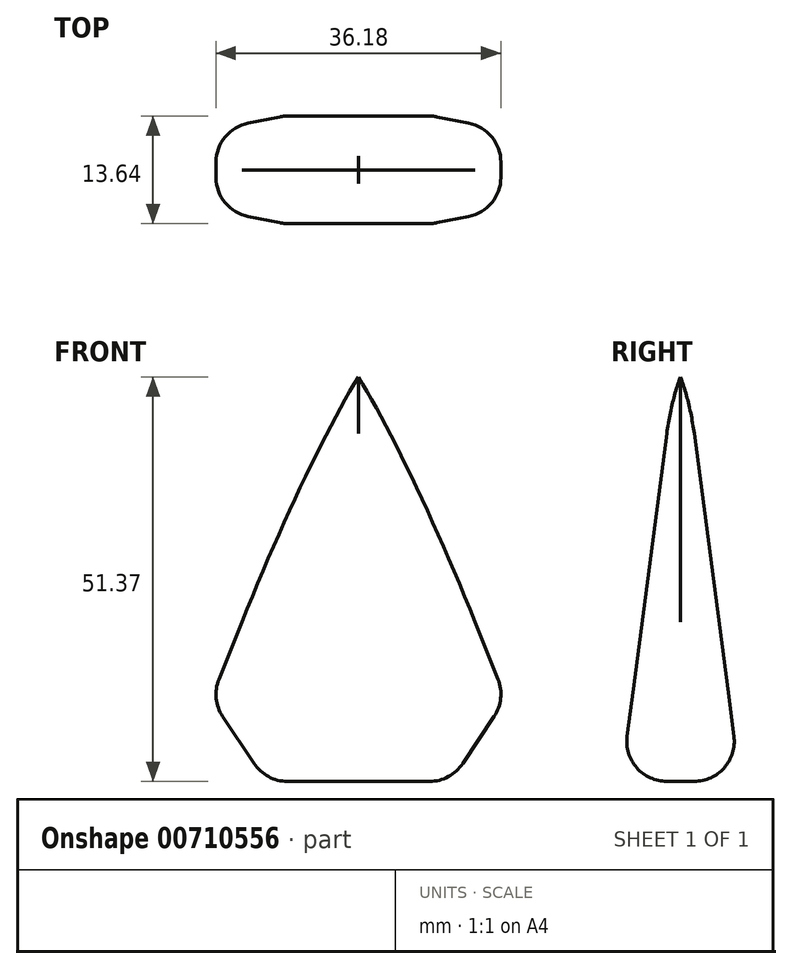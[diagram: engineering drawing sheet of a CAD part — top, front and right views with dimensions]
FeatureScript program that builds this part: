
annotation { "Feature Type Name" : "Feature", "Feature Type Description" : "" }
export const myFeature = defineFeature(function(context is Context, id is Id, definition is map)
    precondition{}
    {
        {
            var Q0;
            Q0=qCreatedBy(makeId("Front.planeOp"),FACE);
            var sketch = newSketch(context, id + "F0", { "sketchPlane" : qUnion([Q0])});
            skLineSegment(sketch, "E0", {"start": v(0, -118.48) * mm, "end": v(-11.74, -118.48) * mm});
            skLineSegment(sketch, "E1", {"start": v(-11.74, -118.48) * mm, "end": v(-18.73, -108) * mm});
            skLineSegment(sketch, "E2", {"start": v(-18.73, -108) * mm, "end": v(0, -61.33) * mm});
            skLineSegment(sketch, "E3", {"start": v(0, -61.33) * mm, "end": v(0, -68.6) * mm});
            skLineSegment(sketch, "E4.MirrorCS", {"start": v(18.73, -108) * mm, "end": v(0, -61.33) * mm});
            skLineSegment(sketch, "E5.MirrorCS", {"start": v(11.74, -118.48) * mm, "end": v(18.73, -108) * mm});
            skLineSegment(sketch, "E6.MirrorCS", {"start": v(0, -118.48) * mm, "end": v(11.74, -118.48) * mm});
            skSolve(sketch);
        }
        {
            var Q0;
            Q0=makeQuery(id+"F0.imprint","IMPRINT",FACE,{"disambiguationData":[TD([[makeQuery(id+"F0.imprint","IMPRINT",EDGE,{"derivedFrom":sQuery(id+"F0.wireOp",EDGE,"E0")}),-1.0]])]});
            extrude(context, id + "F1", {"entities" : qUnion([Q0]), "depth" : 7.62 * mm, "offsetDistance" : 25.4 * mm});
        }
        {
            var Q0;
            Q0=makeQuery(id+"F1.opExtrude","CAP_FACE",FACE,{"disambiguationData":[OSD([sQuery(id+"F0.wireOp",EDGE,"E0"),sQuery(id+"F0.wireOp",EDGE,"E1"),sQuery(id+"F0.wireOp",EDGE,"E2"),sQuery(id+"F0.wireOp",EDGE,"E4.MirrorCS"),sQuery(id+"F0.wireOp",EDGE,"E5.MirrorCS"),sQuery(id+"F0.wireOp",EDGE,"E6.MirrorCS")])],"isStart":true});
            extrude(context, id + "F2", {"entities" : qUnion([Q0]), "operationType" : NewBodyOperationType.ADD, "depth" : 7.62 * mm, "offsetDistance" : 25.4 * mm});
        }
        {
            var Q0;
            Q0=qCreatedBy(makeId("Right.planeOp"),FACE);
            var sketch = newSketch(context, id + "F3", { "sketchPlane" : qUnion([Q0])});
            skLineSegment(sketch, "E7", {"start": v(0, -61.02) * mm, "end": v(-7.8, -120.59) * mm});
            skLineSegment(sketch, "E8", {"start": v(0, -61.02) * mm, "end": v(0, -70.15) * mm});
            skLineSegment(sketch, "E9.MirrorCS", {"start": v(0, -61.02) * mm, "end": v(7.8, -120.59) * mm});
            skLineSegment(sketch, "E10", {"start": v(7.8, -120.59) * mm, "end": v(-7.8, -120.59) * mm});
            skLineSegment(sketch, "E11", {"start": v(-14.15, -128.32) * mm, "end": v(-14.15, -55.45) * mm});
            skLineSegment(sketch, "E12", {"start": v(-14.15, -55.45) * mm, "end": v(17.72, -55.45) * mm});
            skLineSegment(sketch, "E13", {"start": v(17.72, -55.45) * mm, "end": v(15.55, -132.5) * mm});
            skLineSegment(sketch, "E14", {"start": v(15.55, -132.5) * mm, "end": v(-14.15, -128.32) * mm});
            skSolve(sketch);
        }
        {
            var Q0;
            Q0=makeQuery(id+"F3.imprint","IMPRINT",FACE,{"disambiguationData":[TD([[makeQuery(id+"F3.imprint","IMPRINT",EDGE,{"derivedFrom":sQuery(id+"F3.wireOp",EDGE,"E7")}),-1.0]])]});
            extrude(context, id + "F4", {"entities" : qUnion([Q0]), "operationType" : NewBodyOperationType.REMOVE, "oppositeDirection" : true, "depth" : 25.4 * mm, "offsetDistance" : 25.4 * mm});
        }
        {
            var Q0;
            {var subQ4=sQuery(id+"F3.wireOp",EDGE,"E9.MirrorCS");Q0=makeQuery(id+"F4.boolean.opBoolean","COPY",FACE,{"disambiguationData":[TD([makeQuery(id+"F4.opExtrude","SWEPT_FACE",FACE,{"disambiguationData":[OSD([subQ4])]})])],"derivedFrom":makeQuery(id+"F4.opExtrude","CAP_FACE",FACE,{"disambiguationData":[OSD([sQuery(id+"F3.wireOp",EDGE,"E7"),subQ4,sQuery(id+"F3.wireOp",EDGE,"E10"),sQuery(id+"F3.wireOp",EDGE,"E11"),sQuery(id+"F3.wireOp",EDGE,"E12"),sQuery(id+"F3.wireOp",EDGE,"E13"),sQuery(id+"F3.wireOp",EDGE,"E14")])],"isStart":true})});}
            extrude(context, id + "F5", {"entities" : qUnion([Q0]), "operationType" : NewBodyOperationType.REMOVE, "oppositeDirection" : true, "depth" : 25.4 * mm, "offsetDistance" : 25.4 * mm});
        }
        {
            var Q0;
            {var subQ4=sQuery(id+"F3.wireOp",EDGE,"E7");Q0=makeQuery(id+"F4.boolean.opBoolean","COPY",FACE,{"disambiguationData":[TD([makeQuery(id+"F4.opExtrude","SWEPT_FACE",FACE,{"disambiguationData":[OSD([subQ4])]})])],"derivedFrom":makeQuery(id+"F4.opExtrude","CAP_FACE",FACE,{"disambiguationData":[OSD([subQ4,sQuery(id+"F3.wireOp",EDGE,"E9.MirrorCS"),sQuery(id+"F3.wireOp",EDGE,"E10"),sQuery(id+"F3.wireOp",EDGE,"E11"),sQuery(id+"F3.wireOp",EDGE,"E12"),sQuery(id+"F3.wireOp",EDGE,"E13"),sQuery(id+"F3.wireOp",EDGE,"E14")])],"isStart":true})});}
            extrude(context, id + "F6", {"entities" : qUnion([Q0]), "operationType" : NewBodyOperationType.REMOVE, "oppositeDirection" : true, "depth" : 25.4 * mm, "offsetDistance" : 25.4 * mm});
        }
        {
            var Q0;
            {var subQ0=sQuery(id+"F3.wireOp",EDGE,"E7");Q0=makeQuery(id+"F6.boolean.opBoolean","MERGE",FACE,{"derivedFrom":[makeQuery(id+"F4.boolean.opBoolean","COPY",FACE,{"derivedFrom":makeQuery(id+"F4.opExtrude","SWEPT_FACE",FACE,{"disambiguationData":[OSD([subQ0])]})})],"fromTools":[makeQuery(id+"F6.opExtrude","SWEPT_FACE",FACE,{"disambiguationData":[OSD([subQ0])]})]});}
            var Q1;
            {var subQ0=sQuery(id+"F3.wireOp",EDGE,"E9.MirrorCS");Q1=makeQuery(id+"F5.boolean.opBoolean","MERGE",FACE,{"derivedFrom":[makeQuery(id+"F4.boolean.opBoolean","COPY",FACE,{"derivedFrom":makeQuery(id+"F4.opExtrude","SWEPT_FACE",FACE,{"disambiguationData":[OSD([subQ0])]})})],"fromTools":[makeQuery(id+"F5.opExtrude","SWEPT_FACE",FACE,{"disambiguationData":[OSD([subQ0])]})]});}
            var Q2;
            {var subQ0=sQuery(id+"F0.wireOp",EDGE,"E1");Q2=makeQuery(id+"F2.boolean.opBoolean","MERGE",FACE,{"derivedFrom":[makeQuery(id+"F1.opExtrude","SWEPT_FACE",FACE,{"disambiguationData":[OSD([subQ0])]}),makeQuery(id+"F2.opExtrude","SWEPT_FACE",FACE,{"disambiguationData":[OSD([subQ0])]})]});}
            var Q3;
            {var subQ0=sQuery(id+"F0.wireOp",EDGE,"E5.MirrorCS");Q3=makeQuery(id+"F2.boolean.opBoolean","MERGE",FACE,{"derivedFrom":[makeQuery(id+"F1.opExtrude","SWEPT_FACE",FACE,{"disambiguationData":[OSD([subQ0])]}),makeQuery(id+"F2.opExtrude","SWEPT_FACE",FACE,{"disambiguationData":[OSD([subQ0])]})]});}
            var Q4;
            {var subQ0=sQuery(id+"F0.wireOp",EDGE,"E6.MirrorCS");var subQ1=sQuery(id+"F0.wireOp",EDGE,"E0");Q4=makeQuery(id+"F2.boolean.opBoolean","MERGE",FACE,{"derivedFrom":[makeQuery(id+"F1.opExtrude","SWEPT_FACE",FACE,{"disambiguationData":[OSD([subQ1,subQ0])]}),makeQuery(id+"F2.opExtrude","SWEPT_FACE",FACE,{"disambiguationData":[OSD([subQ1,subQ0])]})]});}
            fillet(context, id + "F7", {"entities" : qUnion([Q0, Q1, Q2, Q3, Q4]), "radius" : 5.08 * mm, "tangentPropagation" : true, "allowEdgeOverflow" : false});
        }
    });
